# Revit family: 3DCAD_LGH-15_100RVX3-E
name_source: partatom
category: 機械設備
revit_build: Autodesk Revit 2018 (Build: 20180423_1000(x64)
units: mm (PartAtom-declared; Revit-internal decimal feet)

## family parameters
OmniClass タイトル = Climate Control (HVAC)
OmniClass 番号 = 23.75.00.00
パーツ タイプ = 標準
ロード時にボイドで切り取り = いいえ
丸型コネクタ寸法 = 直径を使用
作業面ベース = いいえ
共有 = いいえ
常に垂直 = はい
部屋計算ポイント = いいえ

## types (14) — shared parameters
Space View = はい
URL = http://global.mitsubishielectric.com
製造元 = Mitsubishi Electric Corporation
説明 = LOSSNAY

## per-type parameters (varying)
| type | Air pipe_Length | Air pipe_diameter 1 | Air pipe_diameter 2 | Box_H | Box_W | Center Height | D | Distance of Air pipes | Distance of Center Height and Air pipes | Electrical power supply | H | Hertz | Mounting pitch 1 | Mounting pitch 2 | Upper Unit-LEG Distance | W | Weight | モデル |
| LGH-15RVX3-E_50Hz | 54  [stored 0.177165 ft] | 98 | 110  [stored 0.360892 ft] | 11 | 37 | 145 | 780 | 450  [stored 1.47638 ft] | 50  [stored 0.164042 ft] | 220-240 V | 289  [stored 0.948163 ft] | 50.0 Hz | 658  [stored 2.15879 ft] | 768  [stored 2.51969 ft] | 65  [stored 0.213255 ft] | 610  [stored 2.00131 ft] | 20.00 kg | LGH-15RVX3-E |
| LGH-25RVX3-E_50Hz | 64  [stored 0.209974 ft] | 142  [stored 0.465879 ft] | 160  [stored 0.524934 ft] | 11 | 37 | 145 | 780 | 530  [stored 1.73885 ft] | 30  [stored 0.0984252 ft] | 220-240 V | 289  [stored 0.948163 ft] | 50.0 Hz | 782 | 768  [stored 2.51969 ft] | 65  [stored 0.213255 ft] | 735 | 22.00 kg | LGH-25RVX3-E |
| LGH-35RVX3-E_50Hz | 64  [stored 0.209974 ft] | 142  [stored 0.465879 ft] | 160  [stored 0.524934 ft] | 55  [stored 0.180446 ft] | 71  [stored 0.23294 ft] | 166 | 888 | 650  [stored 2.13255 ft] | 55  [stored 0.180446 ft] | 220-240 V | 331  [stored 1.08596 ft] | 50.0 Hz | 921 | 875 | 85  [stored 0.278871 ft] | 874 | 30.00 kg | LGH-35RVX3-E |
| LGH-50RVX3-E_50Hz | 79 | 192  [stored 0.629921 ft] | 208 | 55  [stored 0.180446 ft] | 71  [stored 0.23294 ft] | 166 | 888 | 745  [stored 2.44423 ft] | 30  [stored 0.0984252 ft] | 220-240 V | 331  [stored 1.08596 ft] | 50.0 Hz | 1063 | 875 | 85  [stored 0.278871 ft] | 1016 | 33.00 kg | LGH-50RVX3-E |
| LGH-65RVX3-E_50Hz | 79 | 192  [stored 0.629921 ft] | 208 | 87 | 54  [stored 0.177165 ft] | 202  [stored 0.66273 ft] | 908 | 692  [stored 2.27034 ft] | 40  [stored 0.131234 ft] | 220-240 V | 404  [stored 1.32546 ft] | 50.0 Hz | 1001 | 895 | 70  [stored 0.229659 ft] | 954 | 41.00 kg | LGH-65RVX3-E |
| LGH-80RVX3-E_50Hz | 79 | 242  [stored 0.793963 ft] | 258  [stored 0.846457 ft] | 96  [stored 0.314961 ft] | 110  [stored 0.360892 ft] | 202  [stored 0.66273 ft] | 1144 | 690  [stored 2.26378 ft] | 40  [stored 0.131234 ft] | 220-240 V | 404  [stored 1.32546 ft] | 50.0 Hz | 1051 | 1131 | 77  [stored 0.252625 ft] | 1004 | 47.00 kg | LGH-80RVX3-E |
| LGH-100RVX3-E_50Hz | 79 | 242  [stored 0.793963 ft] | 258  [stored 0.846457 ft] | 96  [stored 0.314961 ft] | 110  [stored 0.360892 ft] | 202  [stored 0.66273 ft] | 1144 | 917 | 40  [stored 0.131234 ft] | 220-240 V | 404  [stored 1.32546 ft] | 50.0 Hz | 1278 | 1131 | 77  [stored 0.252625 ft] | 1231 | 53.00 kg | LGH-100RVX3-E |
| LGH-15RVX3-E_60Hz | 54  [stored 0.177165 ft] | 98 | 110  [stored 0.360892 ft] | 11 | 37 | 145 | 780 | 450  [stored 1.47638 ft] | 50  [stored 0.164042 ft] | 220 V | 289  [stored 0.948163 ft] | 60.0 Hz | 658  [stored 2.15879 ft] | 768  [stored 2.51969 ft] | 65  [stored 0.213255 ft] | 610  [stored 2.00131 ft] | 20.00 kg | LGH-15RVX3-E |
| LGH-25RVX3-E_60Hz | 64  [stored 0.209974 ft] | 142  [stored 0.465879 ft] | 160  [stored 0.524934 ft] | 11 | 37 | 145 | 780 | 530  [stored 1.73885 ft] | 30  [stored 0.0984252 ft] | 220 V | 289  [stored 0.948163 ft] | 60.0 Hz | 782 | 768  [stored 2.51969 ft] | 65  [stored 0.213255 ft] | 735 | 22.00 kg | LGH-25RVX3-E |
| LGH-35RVX3-E_60Hz | 64  [stored 0.209974 ft] | 142  [stored 0.465879 ft] | 160  [stored 0.524934 ft] | 55  [stored 0.180446 ft] | 71  [stored 0.23294 ft] | 166 | 888 | 650  [stored 2.13255 ft] | 55  [stored 0.180446 ft] | 220 V | 331  [stored 1.08596 ft] | 60.0 Hz | 921 | 875 | 85  [stored 0.278871 ft] | 874 | 30.00 kg | LGH-35RVX3-E |
| LGH-50RVX3-E_60Hz | 79 | 192  [stored 0.629921 ft] | 208 | 55  [stored 0.180446 ft] | 71  [stored 0.23294 ft] | 166 | 888 | 745  [stored 2.44423 ft] | 30  [stored 0.0984252 ft] | 220 V | 331  [stored 1.08596 ft] | 60.0 Hz | 1063 | 875 | 85  [stored 0.278871 ft] | 1016 | 33.00 kg | LGH-50RVX3-E |
| LGH-65RVX3-E_60Hz | 79 | 192  [stored 0.629921 ft] | 208 | 87 | 54  [stored 0.177165 ft] | 202  [stored 0.66273 ft] | 908 | 692  [stored 2.27034 ft] | 40  [stored 0.131234 ft] | 220 V | 404  [stored 1.32546 ft] | 60.0 Hz | 1001 | 895 | 70  [stored 0.229659 ft] | 954 | 41.00 kg | LGH-65RVX3-E |
| LGH-80RVX3-E_60Hz | 79 | 242  [stored 0.793963 ft] | 258  [stored 0.846457 ft] | 96  [stored 0.314961 ft] | 110  [stored 0.360892 ft] | 202  [stored 0.66273 ft] | 1144 | 690  [stored 2.26378 ft] | 40  [stored 0.131234 ft] | 220 V | 404  [stored 1.32546 ft] | 60.0 Hz | 1051 | 1131 | 77  [stored 0.252625 ft] | 1004 | 47.00 kg | LGH-80RVX3-E |
| LGH-100RVX3-E_60Hz | 79 | 242  [stored 0.793963 ft] | 258  [stored 0.846457 ft] | 96  [stored 0.314961 ft] | 110  [stored 0.360892 ft] | 202  [stored 0.66273 ft] | 1144 | 917 | 40  [stored 0.131234 ft] | 220 V | 404  [stored 1.32546 ft] | 60.0 Hz | 1278 | 1131 | 77  [stored 0.252625 ft] | 1231 | 53.00 kg | LGH-100RVX3-E |

note: [stored X ft] marks values corroborated as IEEE doubles in the binary element streams (Revit-internal decimal feet)

## geometry (parser evidence)
native form markers: Blend x2
no freeform markers — native parametric forms only
